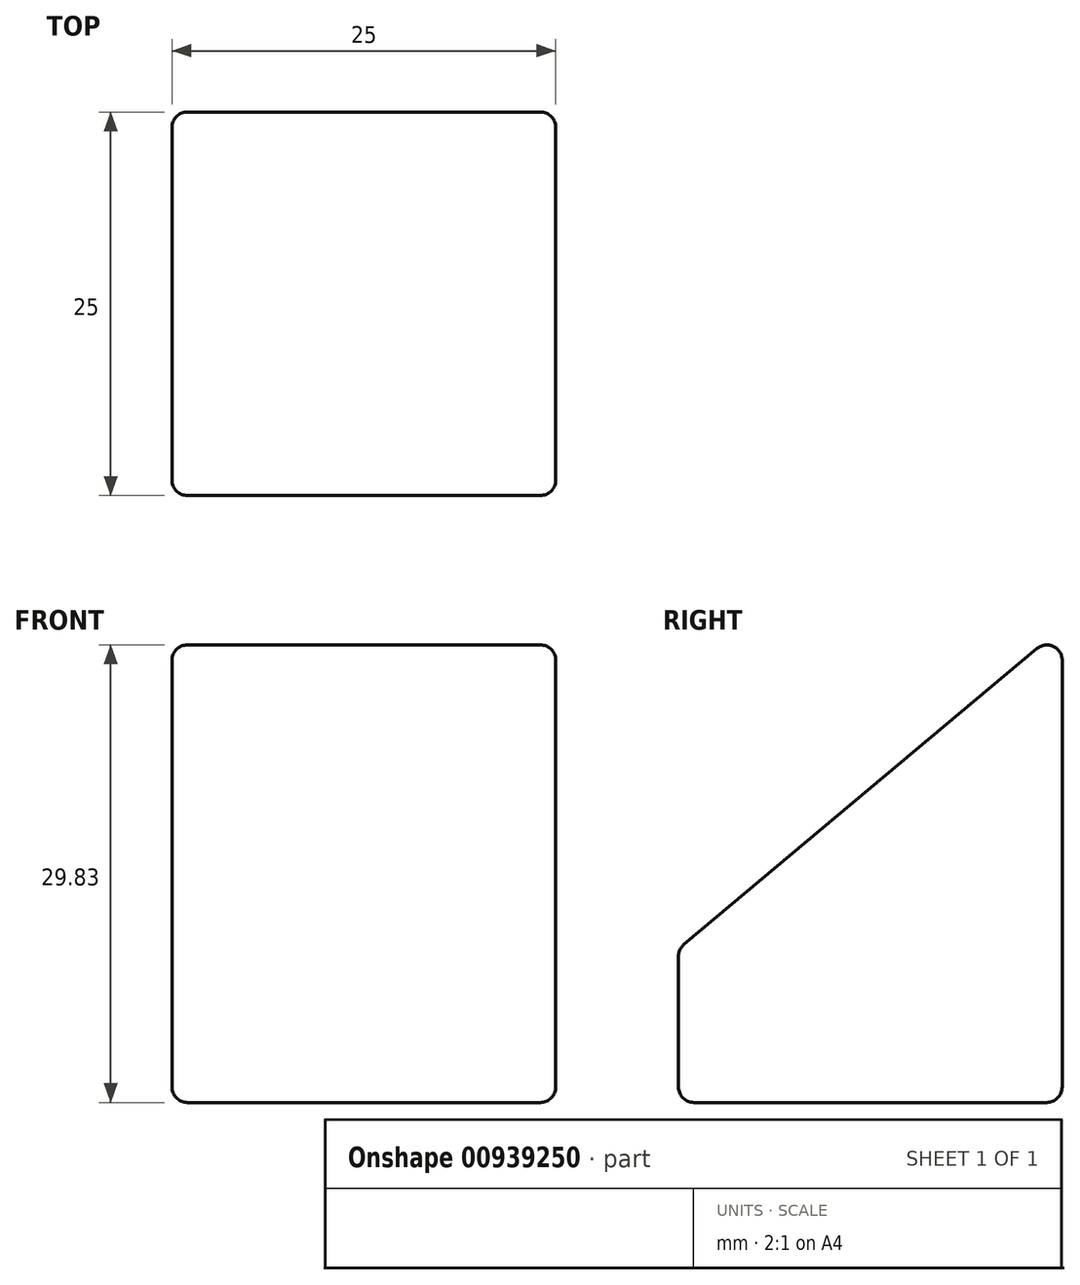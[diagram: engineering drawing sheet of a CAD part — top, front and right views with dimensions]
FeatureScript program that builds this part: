
annotation { "Feature Type Name" : "Feature", "Feature Type Description" : "" }
export const myFeature = defineFeature(function(context is Context, id is Id, definition is map)
    precondition{}
    {
        {
            var Q0;
            Q0=qCreatedBy(makeId("Right.planeOp"),FACE);
            var sketch = newSketch(context, id + "F0", { "sketchPlane" : qUnion([Q0])});
            skLineSegment(sketch, "E0", {"start": v(0, 0) * mm, "end": v(-25, 0) * mm});
            skLineSegment(sketch, "E1", {"start": v(-25, 0) * mm, "end": v(-25, 10) * mm});
            skLineSegment(sketch, "E2", {"start": v(-25, 10) * mm, "end": v(0, 30.98) * mm});
            skLineSegment(sketch, "E3", {"start": v(0, 30.98) * mm, "end": v(0, 0) * mm});
            skSolve(sketch);
        }
        {
            var Q0;
            Q0=makeQuery(id+"F0.imprint","IMPRINT",FACE,{"disambiguationData":[TD([[makeQuery(id+"F0.imprint","IMPRINT",EDGE,{"derivedFrom":sQuery(id+"F0.wireOp",EDGE,"E0")}),-1.0]])]});
            extrude(context, id + "F1", {"entities" : qUnion([Q0]), "depth" : 25 * mm, "offsetDistance" : 25 * mm});
        }
        {
            var Q0;
            Q0=makeQuery(id+"F1.opExtrude","SWEPT_FACE",FACE,{"disambiguationData":[OSD([sQuery(id+"F0.wireOp",EDGE,"E3")])]});
            var Q1;
            Q1=makeQuery(id+"F1.opExtrude","SWEPT_FACE",FACE,{"disambiguationData":[OSD([sQuery(id+"F0.wireOp",EDGE,"E2")])]});
            var Q2;
            Q2=makeQuery(id+"F1.opExtrude","SWEPT_FACE",FACE,{"disambiguationData":[OSD([sQuery(id+"F0.wireOp",EDGE,"E1")])]});
            var Q3;
            Q3=makeQuery(id+"F1.opExtrude","CAP_FACE",FACE,{"disambiguationData":[OSD([sQuery(id+"F0.wireOp",EDGE,"E0"),sQuery(id+"F0.wireOp",EDGE,"E1"),sQuery(id+"F0.wireOp",EDGE,"E2"),sQuery(id+"F0.wireOp",EDGE,"E3")])],"isStart":false});
            var Q4;
            Q4=makeQuery(id+"F1.opExtrude","CAP_FACE",FACE,{"disambiguationData":[OSD([sQuery(id+"F0.wireOp",EDGE,"E0"),sQuery(id+"F0.wireOp",EDGE,"E1"),sQuery(id+"F0.wireOp",EDGE,"E2"),sQuery(id+"F0.wireOp",EDGE,"E3")])],"isStart":true});
            var Q5;
            Q5=makeQuery(id+"F1.opExtrude","SWEPT_FACE",FACE,{"disambiguationData":[OSD([sQuery(id+"F0.wireOp",EDGE,"E0")])]});
            fillet(context, id + "F2", {"entities" : qUnion([Q0, Q1, Q2, Q3, Q4, Q5]), "radius" : 1 * mm, "tangentPropagation" : true, "allowEdgeOverflow" : false});
        }
    });
